# Revit family: Accessory-Cabinet_Pull-KOHLER-Forte-K-11285
name_source: partatom
category: Specialty Equipment
revit_build: Autodesk Revit 2015 (Build: 20140606_1530(x64)
units: mm (PartAtom-declared; Revit-internal decimal feet)

## types (3) — shared parameters
ADA Compliant = No
Assembly Code = C1030200
Date Modified = 11/28/2018
Default Elevation = 42"
Description = 3 Inch Drawer pull
Height = 7/8"
Length = 3 7/8"
Manufacturer = KOHLER Co.
MasterFormat 1995 = 10820
MasterFormat 2004 = 10.28.13
Material = Premium Metal Construction
Product Documentation Link = http://www.us.kohler.com
Product Name = Forte
Product Page URL = http://www.us.kohler.com
URL = https://www.us.kohler.com
Width = 1 5/16"

## per-type parameters (varying)
| type | Finish | Model | Type |
| CP-Polished Chrome | Kohler-Metal-CP-Polished_Chrome | K-11285-CP | 1 |
| G-Brushed Chrome | Kohler-Metal-G-Brushed_Chrome | K-11285-G | 2 |
| BN-Vibrant Brushed Nickel | Kohler-Metal-BN-Vibrant_Brushed_Nickel | K-11285-BN | 3 |

## geometry (parser evidence)
native form markers: Sweep x5
no freeform markers — native parametric forms only
